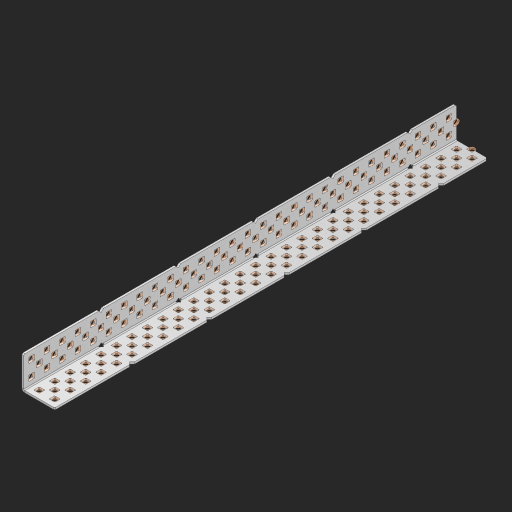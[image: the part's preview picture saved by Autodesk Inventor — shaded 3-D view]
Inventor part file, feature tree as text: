
AUTODESK INVENTOR PART (.ipt)
format: ipt  version: 2023 (Build 270158000, 158)  size: 1,975,296 bytes
history: native  units: in
note: dims shown in document units (in); Inventor stores cm internally (conversion verified against a paired STEP export)
features: other x174, extrude x166, sheet_metal_op x8, sketch x7, pattern_linear x2, mirror x1, chamfer x1
ambient origin geometry x8: Origin, YZ Plane, XZ Plane, XY Plane, X Axis, Y Axis, Z Axis, Center Point
bodies: Solid1 (feature_tree), Body (feature_tree)
feature tree (359):
  sheet_metal_op  "Flanges"
  sheet_metal_op  "Body Pattern"
  pattern_linear  "Center Pattern"  Spacing1=1.0in  [1 undecoded]
  other  "Arc Length"
  pattern_linear  "Notch Pattern"  Spacing1=0.25in  [1 undecoded]
  other  "Diagonal Plane"
  mirror  "Everything Mirrored"
  chamfer  "End Chamfer"
  sketch  "Sketch1"  dims[d0=1.0in]
  other  "Plate1"
  sketch  "Sketch2"  dims[d1=14.0in]
  other  "Plate2"
  sheet_metal_op  "Bend1"
  sheet_metal_op  "Corner1"
  sketch  "Sketch8"  dims[d2=0.0625in]
  sketch  "Sketch9"  dims[d3=0.0625in]
  other  "Srf91"
  sheet_metal_op  "Body Pattern Sketch"
  other  "Srf92"
  sketch  "Sketch13"  dims[d4=0.0312in]
  sketch  "Sketch15"  dims[d5=0.125in]
  sketch  "Sketch16"  dims[d6=0.0625in d7=1.0in d8=90.0deg d9=0.0312in d10=0.25in d11=0.0625in d12=0.0625in d49=0.182in d50=0.02in d52=0.25in d53=0.0625in d54=0.0in d55=0.172in d56=1.0in d57=0.0in d60=11.0236in d62=0.5in d63=0.7874in d65=0.5in d85=0.1473in d86=0.1782in d89=0.0625in d90=0.0in d91=0.04in d92=0.0491in d95=2.5in d96=0.04in d97=0.25in d98=45.0deg d99=0.25in d106=0.182in d107=0.02in d108=0.5in d110=0.0625in d111=0.0in d112=0.172in d113=0.5in d114=0.0in d117=0.5in d123=0.25in d125=0.25in d126=0.0491in d127=0.1473in d128=0.08in d129=0.04in d130=2.5in]
  other  "Srf786"
  other  "Srf856"
  other  "Srf857"
  other  "Srf858"
  other  "Srf859"
  other  "Srf860"
  other  "Srf861"
  other  "Srf889"
  other  "Srf890"
  other  "Srf891"
  other  "Srf1275"
  other  "Srf1276"
  other  "Srf1278"
  other  "Srf1279"
  other  "Srf1280"
  other  "Srf1281"
  other  "Srf1282"
  other  "Srf1283"
  other  "Srf1277"
  other  "Srf1285"
  other  "Srf1286"
  other  "Srf1287"
  other  "Srf1383"
  other  "Srf1384"
  other  "Srf1385"
  other  "Srf1386"
  other  "Srf1387"
  other  "Srf1388"
  other  "Srf1389"
  other  "Srf1390"
  other  "Srf1391"
  other  "Srf1392"
  other  "Srf1393"
  other  "Srf1394"
  other  "Srf1395"
  other  "Srf1396"
  other  "Srf1397"
  other  "Srf1398"
  other  "Srf1399"
  other  "Srf1400"
  other  "Srf1401"
  other  "Srf1402"
  other  "Srf1403"
  other  "Srf1404"
  other  "Srf1405"
  other  "Srf1406"
  other  "Srf1407"
  other  "Srf1408"
  other  "Srf1409"
  other  "Srf1410"
  other  "Srf1411"
  other  "Srf1412"
  other  "Srf1413"
  other  "Srf1414"
  other  "Srf1415"
  other  "Srf1416"
  other  "Srf1417"
  other  "Srf1418"
  other  "Srf1419"
  other  "Srf1420"
  other  "Srf1421"
  other  "Srf1422"
  other  "Srf1423"
  other  "Srf1424"
  other  "Srf1425"
  other  "Srf1426"
  other  "Srf1427"
  other  "Srf1428"
  other  "Srf1429"
  other  "Srf1430"
  other  "Srf1445"
  other  "Srf1446"
  other  "Srf1447"
  other  "Srf1448"
  other  "Srf1449"
  other  "Srf1450"
  other  "Srf1451"
  other  "Srf1452"
  other  "Srf1453"
  other  "Srf1454"
  other  "Srf1455"
  other  "Srf1456"
  other  "Srf1457"
  other  "Srf1458"
  other  "Srf1459"
  other  "Srf1460"
  other  "Srf1461"
  other  "Srf1462"
  other  "Srf1463"
  other  "Srf1464"
  other  "Srf1465"
  other  "Srf1466"
  other  "Srf1467"
  other  "Srf1468"
  other  "Srf1475"
  other  "Srf1476"
  other  "Srf1477"
  other  "Srf1478"
  other  "Srf1479"
  other  "Srf1480"
  other  "Srf1481"
  other  "Srf1482"
  other  "Srf1483"
  other  "Srf1484"
  other  "Srf1485"
  other  "Srf1486"
  other  "Srf1487"
  other  "Srf1488"
  other  "Srf1489"
  other  "Srf1490"
  other  "Srf1491"
  other  "Srf1492"
  other  "Srf1493"
  other  "Srf1494"
  other  "Srf1495"
  other  "Srf1496"
  other  "Srf1497"
  other  "Srf1498"
  other  "Srf1499"
  other  "Srf1500"
  other  "Srf1501"
  other  "Srf1502"
  other  "Srf1503"
  other  "Srf1504"
  other  "Srf1505"
  other  "Srf1506"
  other  "Srf1507"
  other  "Srf1508"
  other  "Srf1509"
  other  "Srf1510"
  other  "Srf1511"
  other  "Srf1512"
  other  "Srf1513"
  other  "Srf1514"
  other  "Srf1515"
  other  "Srf1516"
  other  "Srf1517"
  other  "Srf1518"
  other  "Srf1519"
  other  "Srf1520"
  other  "Srf1521"
  other  "Srf1522"
  other  "Srf1537"
  other  "Srf1538"
  other  "Srf1539"
  other  "Srf1540"
  other  "Srf1541"
  other  "Srf1542"
  other  "Srf1543"
  other  "Srf1544"
  other  "Srf1545"
  other  "Srf1546"
  other  "Srf1547"
  other  "Srf1548"
  other  "Srf1549"
  other  "Srf1550"
  other  "Srf1551"
  other  "Srf1552"
  other  "Srf1553"
  other  "Srf1554"
  other  "Srf1555"
  other  "Srf1556"
  other  "Srf1557"
  other  "Srf1558"
  other  "Srf1559"
  other  "Srf1560"
  sheet_metal_op  "Body Stamp"
  sheet_metal_op  "Body Circle"
  other  "Center Stamp"
  other  "Center Circle"
  sheet_metal_op  "Notch"
  extrude  "ExtrusionSrf92"  Depth=0.0625in
  extrude  "ExtrusionSrf856"  Depth=0.0625in
  extrude  "ExtrusionSrf857"  Depth=0.182in
  extrude  "ExtrusionSrf858"  Depth=0.02in
  extrude  "ExtrusionSrf859"  Depth=0.25in
  extrude  "ExtrusionSrf860"  Depth=0.0625in
  extrude  "ExtrusionSrf861"  TaperAngle=0.0deg  [1 undecoded]
  extrude  "ExtrusionSrf889"  Depth=2.5in
  extrude  "ExtrusionSrf890"  Depth=1.0in TaperAngle=0.0deg
  extrude  "ExtrusionSrf891"  Depth=2.5in
  extrude  "ExtrusionSrf1275"  Depth=0.5in
  extrude  "ExtrusionSrf1276"  Depth=2.5in
  extrude  "ExtrusionSrf1277"  Depth=2.5in
  extrude  "ExtrusionSrf1278"  Depth=0.0625in
  extrude  "ExtrusionSrf1279"  Depth=2.5in TaperAngle=0.0deg
  extrude  "ExtrusionSrf1280"  Depth=2.5in
  extrude  "ExtrusionSrf1281"  Depth=0.25in TaperAngle=45.0deg
  extrude  "ExtrusionSrf1282"  Depth=0.25in
  extrude  "ExtrusionSrf1345"  Depth=0.182in
  extrude  "ExtrusionSrf1346"  Depth=0.02in
  extrude  "ExtrusionSrf1347"  Depth=0.5in
  extrude  "ExtrusionSrf1348"  Depth=0.0625in
  extrude  "ExtrusionSrf1383"  TaperAngle=0.0deg  [1 undecoded]
  extrude  "ExtrusionSrf1384"  Depth=2.5in
  extrude  "ExtrusionSrf1385"  Depth=0.5in TaperAngle=0.0deg
  extrude  "ExtrusionSrf1386"  Depth=0.5in
  extrude  "ExtrusionSrf1387"  Depth=0.25in
  extrude  "ExtrusionSrf1388"  Depth=0.25in
  extrude  "ExtrusionSrf1389"  Depth=2.5in
  extrude  "ExtrusionSrf1390"  Depth=2.5in
  extrude  "ExtrusionSrf1391"  Depth=2.5in
  extrude  "ExtrusionSrf1392"  Depth=2.5in
  extrude  "ExtrusionSrf1393"  Depth=2.5in
  extrude  "ExtrusionSrf1394"  [1 undecoded]
  extrude  "ExtrusionSrf1395"  [1 undecoded]
  extrude  "ExtrusionSrf1396"  [1 undecoded]
  extrude  "ExtrusionSrf1397"  [1 undecoded]
  extrude  "ExtrusionSrf1398"  [1 undecoded]
  extrude  "ExtrusionSrf1399"  [1 undecoded]
  extrude  "ExtrusionSrf1400"  [1 undecoded]
  extrude  "ExtrusionSrf1401"  [1 undecoded]
  extrude  "ExtrusionSrf1402"  [1 undecoded]
  extrude  "ExtrusionSrf1403"  [1 undecoded]
  extrude  "ExtrusionSrf1404"  [1 undecoded]
  extrude  "ExtrusionSrf1405"  [1 undecoded]
  extrude  "ExtrusionSrf1406"  [1 undecoded]
  extrude  "ExtrusionSrf1407"  [1 undecoded]
  extrude  "ExtrusionSrf1408"  [1 undecoded]
  extrude  "ExtrusionSrf1409"  [1 undecoded]
  extrude  "ExtrusionSrf1410"  [1 undecoded]
  extrude  "ExtrusionSrf1411"  [1 undecoded]
  extrude  "ExtrusionSrf1412"  [1 undecoded]
  extrude  "ExtrusionSrf1413"  [1 undecoded]
  extrude  "ExtrusionSrf1414"  [1 undecoded]
  extrude  "ExtrusionSrf1415"  [1 undecoded]
  extrude  "ExtrusionSrf1416"  [1 undecoded]
  extrude  "ExtrusionSrf1417"  [1 undecoded]
  extrude  "ExtrusionSrf1418"  [1 undecoded]
  extrude  "ExtrusionSrf1419"  [1 undecoded]
  extrude  "ExtrusionSrf1420"  [1 undecoded]
  extrude  "ExtrusionSrf1421"  [1 undecoded]
  extrude  "ExtrusionSrf1422"  [1 undecoded]
  extrude  "ExtrusionSrf1423"  [1 undecoded]
  extrude  "ExtrusionSrf1424"  [1 undecoded]
  extrude  "ExtrusionSrf1425"  [1 undecoded]
  extrude  "ExtrusionSrf1426"  [1 undecoded]
  extrude  "ExtrusionSrf1427"  [1 undecoded]
  extrude  "ExtrusionSrf1428"  [1 undecoded]
  extrude  "ExtrusionSrf1429"  [1 undecoded]
  extrude  "ExtrusionSrf1430"  [1 undecoded]
  extrude  "ExtrusionSrf1445"  [1 undecoded]
  extrude  "ExtrusionSrf1446"  [1 undecoded]
  extrude  "ExtrusionSrf1447"  [1 undecoded]
  extrude  "ExtrusionSrf1448"  [1 undecoded]
  extrude  "ExtrusionSrf1449"  [1 undecoded]
  extrude  "ExtrusionSrf1450"  [1 undecoded]
  extrude  "ExtrusionSrf1451"  [1 undecoded]
  extrude  "ExtrusionSrf1452"  [1 undecoded]
  extrude  "ExtrusionSrf1453"  [1 undecoded]
  extrude  "ExtrusionSrf1454"  [1 undecoded]
  extrude  "ExtrusionSrf1455"  [1 undecoded]
  extrude  "ExtrusionSrf1456"  [1 undecoded]
  extrude  "ExtrusionSrf1457"  [1 undecoded]
  extrude  "ExtrusionSrf1458"  [1 undecoded]
  extrude  "ExtrusionSrf1459"  [1 undecoded]
  extrude  "ExtrusionSrf1460"  [1 undecoded]
  extrude  "ExtrusionSrf1461"  [1 undecoded]
  extrude  "ExtrusionSrf1462"  [1 undecoded]
  extrude  "ExtrusionSrf1463"  [1 undecoded]
  extrude  "ExtrusionSrf1464"  [1 undecoded]
  extrude  "ExtrusionSrf1465"  [1 undecoded]
  extrude  "ExtrusionSrf1466"  [1 undecoded]
  extrude  "ExtrusionSrf1467"  [1 undecoded]
  extrude  "ExtrusionSrf1468"  [1 undecoded]
  extrude  "ExtrusionSrf1475"  [1 undecoded]
  extrude  "ExtrusionSrf1476"  [1 undecoded]
  extrude  "ExtrusionSrf1477"  [1 undecoded]
  extrude  "ExtrusionSrf1478"  [1 undecoded]
  extrude  "ExtrusionSrf1479"  [1 undecoded]
  extrude  "ExtrusionSrf1480"  [1 undecoded]
  extrude  "ExtrusionSrf1481"  [1 undecoded]
  extrude  "ExtrusionSrf1482"  [1 undecoded]
  extrude  "ExtrusionSrf1483"  [1 undecoded]
  extrude  "ExtrusionSrf1484"  [1 undecoded]
  extrude  "ExtrusionSrf1485"  [1 undecoded]
  extrude  "ExtrusionSrf1486"  [1 undecoded]
  extrude  "ExtrusionSrf1487"  [1 undecoded]
  extrude  "ExtrusionSrf1488"  [1 undecoded]
  extrude  "ExtrusionSrf1489"  [1 undecoded]
  extrude  "ExtrusionSrf1490"  [1 undecoded]
  extrude  "ExtrusionSrf1491"  [1 undecoded]
  extrude  "ExtrusionSrf1492"  [1 undecoded]
  extrude  "ExtrusionSrf1493"  [1 undecoded]
  extrude  "ExtrusionSrf1494"  [1 undecoded]
  extrude  "ExtrusionSrf1495"  [1 undecoded]
  extrude  "ExtrusionSrf1496"  [1 undecoded]
  extrude  "ExtrusionSrf1497"  [1 undecoded]
  extrude  "ExtrusionSrf1498"  [1 undecoded]
  extrude  "ExtrusionSrf1499"  [1 undecoded]
  extrude  "ExtrusionSrf1500"  [1 undecoded]
  extrude  "ExtrusionSrf1501"  [1 undecoded]
  extrude  "ExtrusionSrf1502"  [1 undecoded]
  extrude  "ExtrusionSrf1503"  [1 undecoded]
  extrude  "ExtrusionSrf1504"  [1 undecoded]
  extrude  "ExtrusionSrf1505"  [1 undecoded]
  extrude  "ExtrusionSrf1506"  [1 undecoded]
  extrude  "ExtrusionSrf1507"  [1 undecoded]
  extrude  "ExtrusionSrf1508"  [1 undecoded]
  extrude  "ExtrusionSrf1509"  [1 undecoded]
  extrude  "ExtrusionSrf1510"  [1 undecoded]
  extrude  "ExtrusionSrf1511"  [1 undecoded]
  extrude  "ExtrusionSrf1512"  [1 undecoded]
  extrude  "ExtrusionSrf1513"  [1 undecoded]
  extrude  "ExtrusionSrf1514"  [1 undecoded]
  extrude  "ExtrusionSrf1515"  [1 undecoded]
  extrude  "ExtrusionSrf1516"  [1 undecoded]
  extrude  "ExtrusionSrf1517"  [1 undecoded]
  extrude  "ExtrusionSrf1518"  [1 undecoded]
  extrude  "ExtrusionSrf1519"  [1 undecoded]
  extrude  "ExtrusionSrf1520"  [1 undecoded]
  extrude  "ExtrusionSrf1521"  [1 undecoded]
  extrude  "ExtrusionSrf1522"  [1 undecoded]
  extrude  "ExtrusionSrf1537"  [1 undecoded]
  extrude  "ExtrusionSrf1538"  [1 undecoded]
  extrude  "ExtrusionSrf1539"  [1 undecoded]
  extrude  "ExtrusionSrf1540"  [1 undecoded]
  extrude  "ExtrusionSrf1541"  [1 undecoded]
  extrude  "ExtrusionSrf1542"  [1 undecoded]
  extrude  "ExtrusionSrf1543"  [1 undecoded]
  extrude  "ExtrusionSrf1544"  [1 undecoded]
  extrude  "ExtrusionSrf1545"  [1 undecoded]
  extrude  "ExtrusionSrf1546"  [1 undecoded]
  extrude  "ExtrusionSrf1547"  [1 undecoded]
  extrude  "ExtrusionSrf1548"  [1 undecoded]
  extrude  "ExtrusionSrf1549"  [1 undecoded]
  extrude  "ExtrusionSrf1550"  [1 undecoded]
  extrude  "ExtrusionSrf1551"  [1 undecoded]
  extrude  "ExtrusionSrf1552"  [1 undecoded]
  extrude  "ExtrusionSrf1553"  [1 undecoded]
  extrude  "ExtrusionSrf1554"  [1 undecoded]
  extrude  "ExtrusionSrf1555"  [1 undecoded]
  extrude  "ExtrusionSrf1556"  [1 undecoded]
  extrude  "ExtrusionSrf1557"  [1 undecoded]
  extrude  "ExtrusionSrf1558"  [1 undecoded]
  extrude  "ExtrusionSrf1559"  [1 undecoded]
  extrude  "ExtrusionSrf1560"  [1 undecoded]
note: 137 required parameter values undecoded (feature->parameter linkage not recoverable at this tier; creation-order binding heuristic only, values carry confidence <= 0.55)
